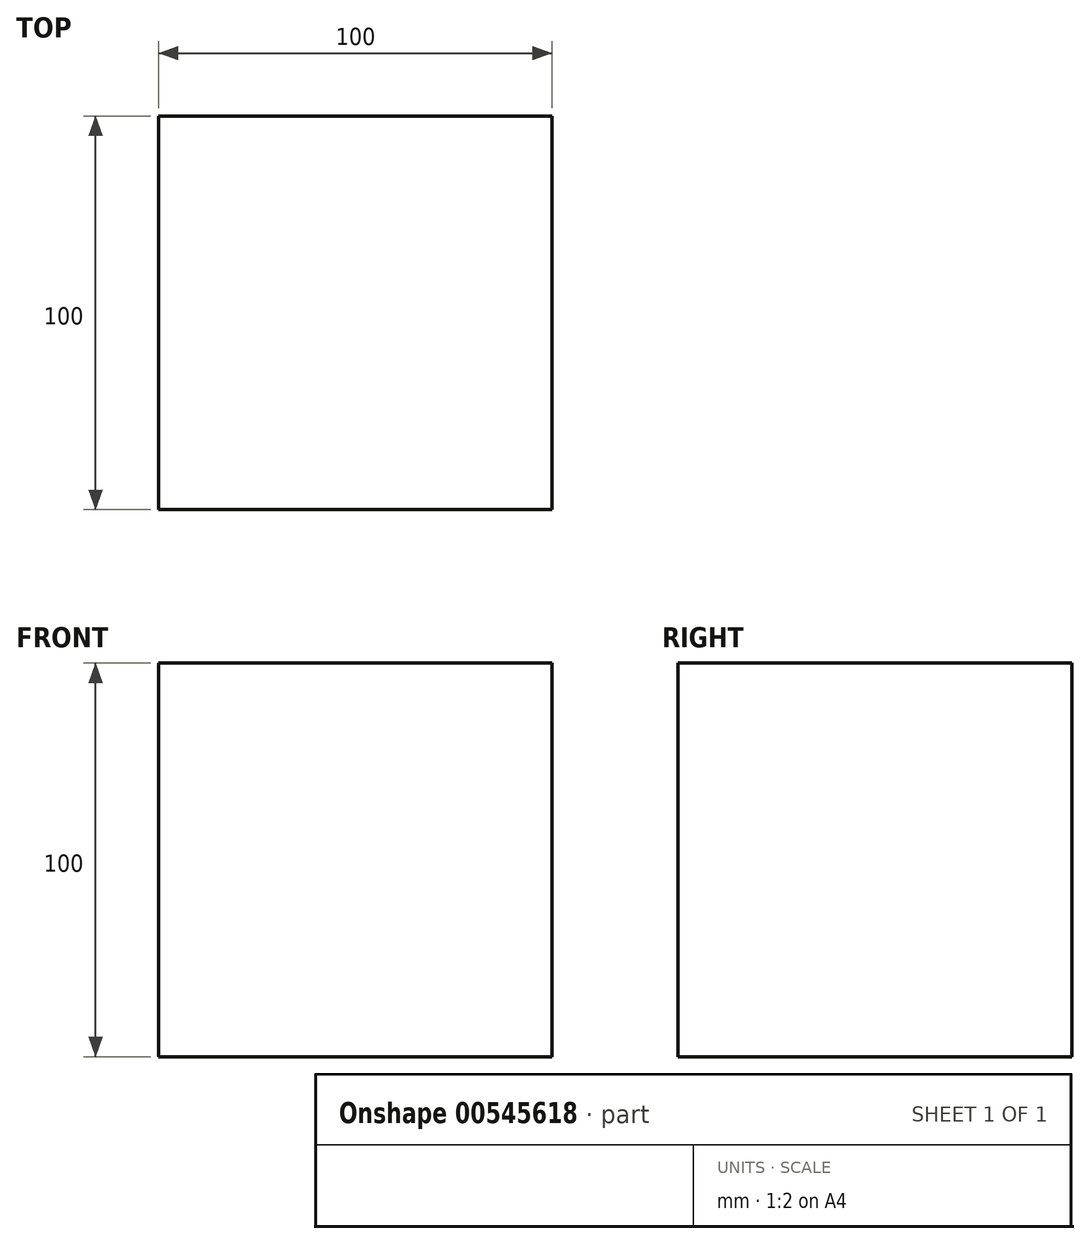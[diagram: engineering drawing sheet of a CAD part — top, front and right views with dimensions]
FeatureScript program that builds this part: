
annotation { "Feature Type Name" : "Feature", "Feature Type Description" : "" }
export const myFeature = defineFeature(function(context is Context, id is Id, definition is map)
    precondition{}
    {
        {
            var Q0;
            Q0=qCreatedBy(makeId("Front.planeOp"),FACE);
            var sketch = newSketch(context, id + "F0", { "sketchPlane" : qUnion([Q0])});
            skLineSegment(sketch, "E0.bottom", {"start": v(-50, 50) * mm, "end": v(50, 50) * mm});
            skLineSegment(sketch, "E0.top", {"start": v(-50, -50) * mm, "end": v(50, -50) * mm});
            skLineSegment(sketch, "E0.left", {"start": v(-50, 50) * mm, "end": v(-50, -50) * mm});
            skLineSegment(sketch, "E0.right", {"start": v(50, 50) * mm, "end": v(50, -50) * mm});
            skSolve(sketch);
        }
        {
            var Q0;
            Q0 = qSketchRegion(id + "F0", true);
            extrude(context, id + "F1", {"entities" : qUnion([Q0]), "depth" : 50 * mm, "offsetDistance" : 25 * mm});
        }
        {
            var Q0;
            Q0 = qSketchRegion(id + "F0", true);
            extrude(context, id + "F2", {"entities" : qUnion([Q0]), "operationType" : NewBodyOperationType.ADD, "oppositeDirection" : true, "depth" : 50 * mm, "offsetDistance" : 25 * mm});
        }
    });
